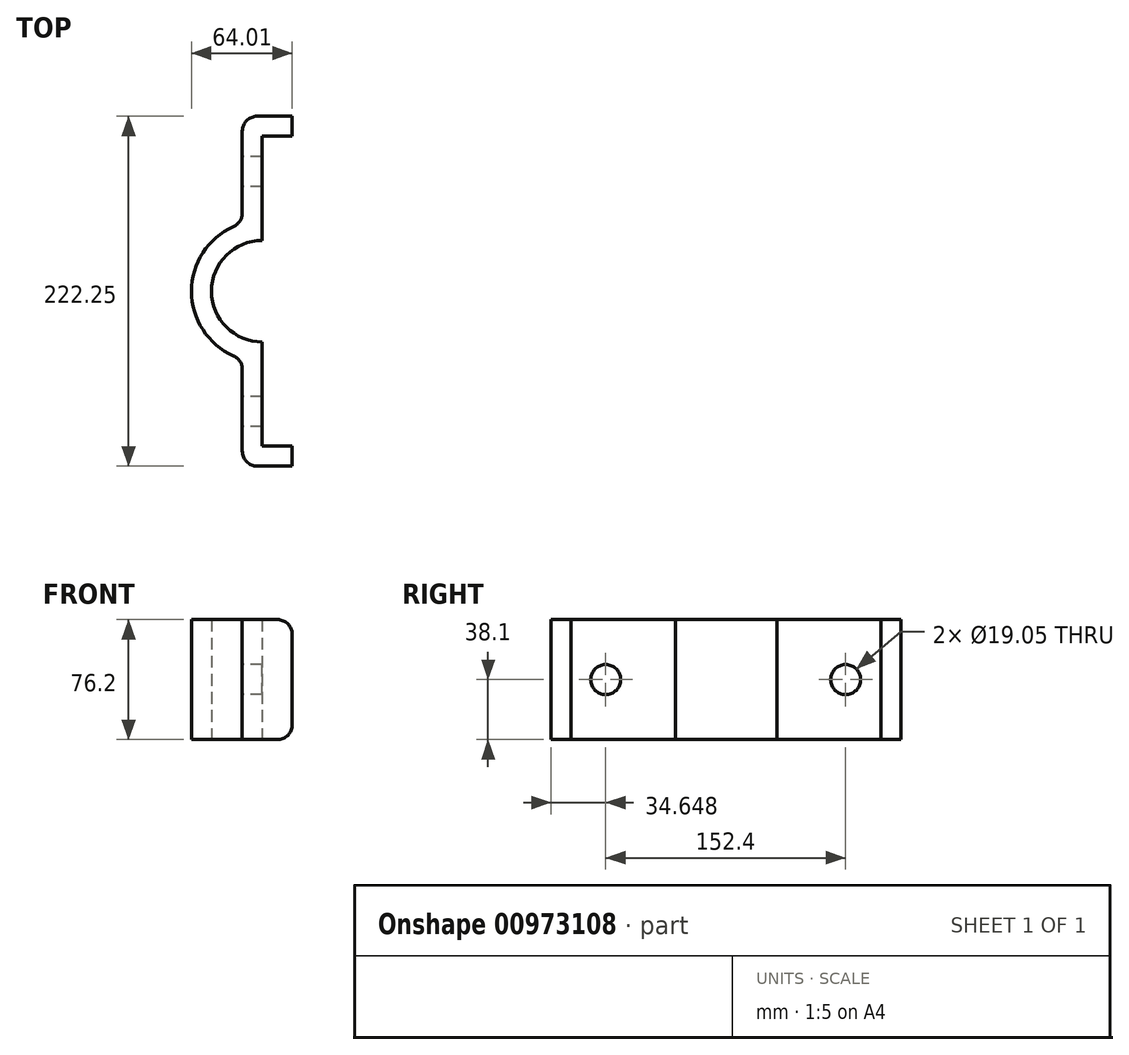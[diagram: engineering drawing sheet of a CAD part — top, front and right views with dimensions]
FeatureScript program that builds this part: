
annotation { "Feature Type Name" : "Feature", "Feature Type Description" : "" }
export const myFeature = defineFeature(function(context is Context, id is Id, definition is map)
    precondition{}
    {
        {
            var Q0;
            Q0=qCreatedBy(makeId("Top.planeOp"),FACE);
            var sketch = newSketch(context, id + "F0", { "sketchPlane" : qUnion([Q0])});
            skLineSegment(sketch, "E0", {"start": v(0, 0) * mm, "end": v(0, 68) * mm});
            skLineSegment(sketch, "E1", {"start": v(0, 222.25) * mm, "end": v(31.75, 222.25) * mm});
            skLineSegment(sketch, "E2", {"start": v(31.75, 222.25) * mm, "end": v(31.75, 209.55) * mm});
            skLineSegment(sketch, "E3", {"start": v(31.75, 209.55) * mm, "end": v(12.7, 209.55) * mm});
            skLineSegment(sketch, "E4", {"start": v(12.7, 209.55) * mm, "end": v(12.7, 143.38) * mm});
            skLineSegment(sketch, "E5", {"start": v(12.7, 12.7) * mm, "end": v(31.75, 12.7) * mm});
            skLineSegment(sketch, "E6", {"start": v(31.75, 12.7) * mm, "end": v(31.75, 0) * mm});
            skLineSegment(sketch, "E7", {"start": v(31.75, 0) * mm, "end": v(0, 0) * mm});
            skArc(sketch, "E8", {"start": v(0, 154.25) * mm, "mid": v(-32.26, 111.13) * mm, "end": v(0, 68) * mm});
            skArc(sketch, "E9", {"start": v(12.7, 143.38) * mm, "mid": v(-19.56, 111.13) * mm, "end": v(12.7, 78.87) * mm});
            skLineSegment(sketch, "E10.trimOffspring", {"start": v(12.7, 78.87) * mm, "end": v(12.7, 12.7) * mm});
            skLineSegment(sketch, "E11.trimOffspring", {"start": v(0, 154.25) * mm, "end": v(0, 222.25) * mm});
            skSolve(sketch);
        }
        {
            var Q0;
            Q0=makeQuery(id+"F0.imprint","IMPRINT",FACE,{"disambiguationData":[TD([[makeQuery(id+"F0.imprint","IMPRINT",EDGE,{"derivedFrom":sQuery(id+"F0.wireOp",EDGE,"E0")}),-1.0]])]});
            extrude(context, id + "F1", {"entities" : qUnion([Q0]), "depth" : 76.2 * mm, "offsetDistance" : 25.4 * mm});
        }
        {
            var Q0;
            Q0=qCreatedBy(makeId("Right.planeOp"),FACE);
            var sketch = newSketch(context, id + "F2", { "sketchPlane" : qUnion([Q0])});
            skCircle(sketch, "E12", {"center": v(187.05, 38.1) * mm, "radius": 9.53 * mm});
            skPoint(sketch, "E13", {"position": v(110.85, 38.1) * mm});
            skCircle(sketch, "E14.MirrorC", {"center": v(34.65, 38.1) * mm, "radius": 9.53 * mm});
            skSolve(sketch);
        }
        {
            var Q0;
            Q0=sQuery(id+"F2.wireOp",VERTEX,"E12.center");
            var Q1;
            Q1=sQuery(id+"F2.wireOp",VERTEX,"E14.MirrorC.center");
            var Q2;
            Q2=makeQuery(id+"F1.opExtrude","SWEPT_BODY",BODY,{"disambiguationData":[OSD([sQuery(id+"F0.wireOp",EDGE,"E0"),sQuery(id+"F0.wireOp",EDGE,"E1"),sQuery(id+"F0.wireOp",EDGE,"E2"),sQuery(id+"F0.wireOp",EDGE,"E3"),sQuery(id+"F0.wireOp",EDGE,"E4"),sQuery(id+"F0.wireOp",EDGE,"E5"),sQuery(id+"F0.wireOp",EDGE,"E6"),sQuery(id+"F0.wireOp",EDGE,"E7"),sQuery(id+"F0.wireOp",EDGE,"E8"),sQuery(id+"F0.wireOp",EDGE,"E9"),sQuery(id+"F0.wireOp",EDGE,"E10.trimOffspring"),sQuery(id+"F0.wireOp",EDGE,"E11.trimOffspring")])]});
            hole(context, id + "F3", {"style" : HoleStyle.SIMPLE, "endStyle" : HoleEndStyle.THROUGH, "oppositeDirection" : true, "holeDiameter" : 19.05 * mm, "majorDiameter" : 6.35 * mm, "isTappedThrough" : true, "tappedDepth" : 12.7 * mm, "tapClearance" : 3, "locations" : qUnion([Q0, Q1]), "scope" : qUnion([Q2])});
        }
        {
            var Q0;
            Q0=makeQuery(id+"F1.opExtrude","SWEPT_EDGE",EDGE,{"disambiguationData":[OSD([sQuery(id+"F0.wireOp",EDGE,"E0"),sQuery(id+"F0.wireOp",EDGE,"E8")])]});
            var Q1;
            Q1=makeQuery(id+"F1.opExtrude","SWEPT_EDGE",EDGE,{"disambiguationData":[OSD([sQuery(id+"F0.wireOp",EDGE,"E8"),sQuery(id+"F0.wireOp",EDGE,"E11.trimOffspring")])]});
            var Q2;
            Q2=makeQuery(id+"F1.opExtrude","SWEPT_EDGE",EDGE,{"disambiguationData":[OSD([sQuery(id+"F0.wireOp",EDGE,"E0"),sQuery(id+"F0.wireOp",EDGE,"E7")])]});
            var Q3;
            Q3=makeQuery(id+"F1.opExtrude","CAP_EDGE",EDGE,{"disambiguationData":[OSD([sQuery(id+"F0.wireOp",EDGE,"E6")])],"isStart":false});
            var Q4;
            Q4=makeQuery(id+"F1.opExtrude","CAP_EDGE",EDGE,{"disambiguationData":[OSD([sQuery(id+"F0.wireOp",EDGE,"E6")])],"isStart":true});
            var Q5;
            Q5=makeQuery(id+"F1.opExtrude","CAP_EDGE",EDGE,{"disambiguationData":[OSD([sQuery(id+"F0.wireOp",EDGE,"E2")])],"isStart":false});
            var Q6;
            Q6=makeQuery(id+"F1.opExtrude","CAP_EDGE",EDGE,{"disambiguationData":[OSD([sQuery(id+"F0.wireOp",EDGE,"E2")])],"isStart":true});
            var Q7;
            Q7=makeQuery(id+"F1.opExtrude","SWEPT_EDGE",EDGE,{"disambiguationData":[OSD([sQuery(id+"F0.wireOp",EDGE,"E1"),sQuery(id+"F0.wireOp",EDGE,"E11.trimOffspring")])]});
            fillet(context, id + "F4", {"entities" : qUnion([Q0, Q1, Q2, Q3, Q4, Q5, Q6, Q7]), "radius" : 9.52 * mm, "tangentPropagation" : true, "allowEdgeOverflow" : false});
        }
    });
